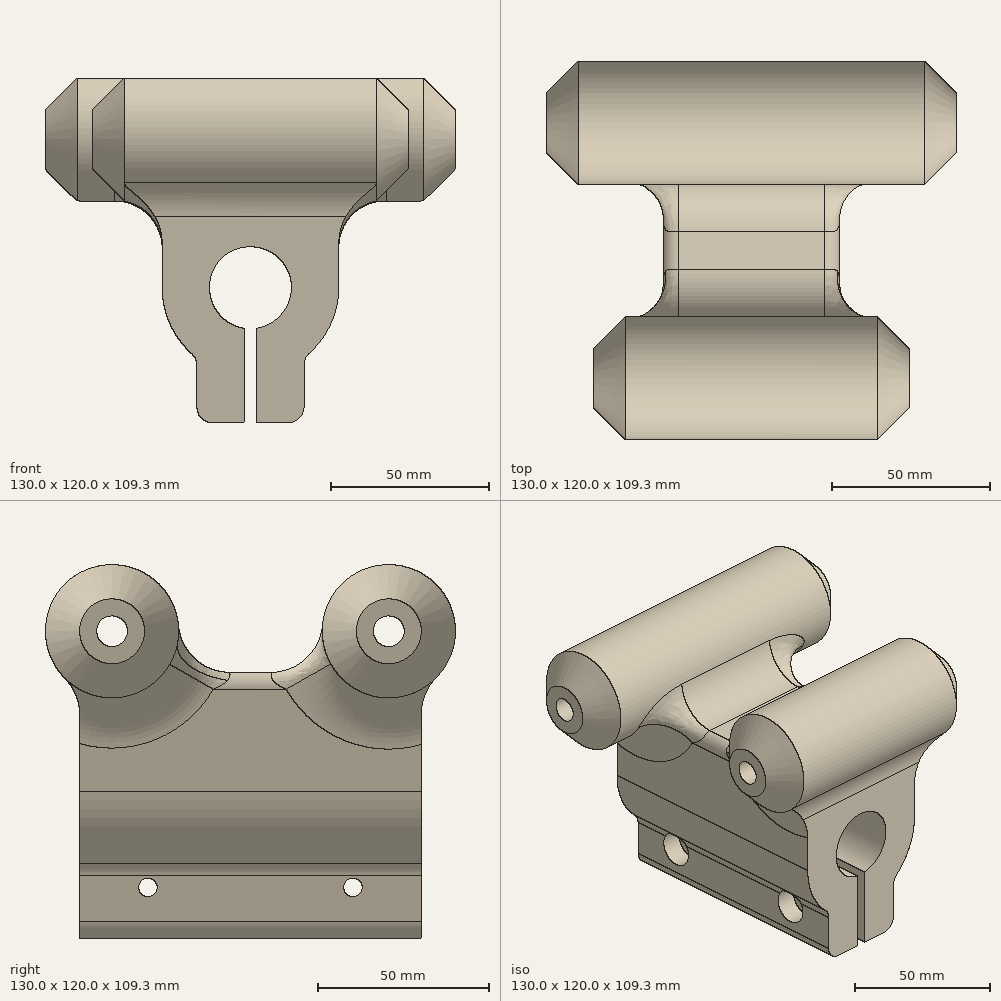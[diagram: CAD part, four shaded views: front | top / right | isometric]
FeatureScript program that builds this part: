
annotation { "Feature Type Name" : "Feature", "Feature Type Description" : "" }
export const myFeature = defineFeature(function(context is Context, id is Id, definition is map)
    precondition{}
    {
        {
            var Q0;
            Q0=qCreatedBy(makeId("Front.planeOp"),FACE);
            var sketch = newSketch(context, id + "F0", { "sketchPlane" : qUnion([Q0])});
            skCircle(sketch, "E0", {"center": v(0, 0) * mm, "radius": 12.5 * mm, "construction": true});
            skCircle(sketch, "E1", {"center": v(0, 0) * mm, "radius": 28 * mm, "construction": true});
            skCircle(sketch, "E2", {"center": v(0, 0) * mm, "radius": 13 * mm, "construction": true});
            skLineSegment(sketch, "E3", {"start": v(-28, 0) * mm, "end": v(-28, 30) * mm});
            skLineSegment(sketch, "E4", {"start": v(-23, 35) * mm, "end": v(23, 35) * mm});
            skLineSegment(sketch, "E5", {"start": v(28, 30) * mm, "end": v(28, 0) * mm});
            skPoint(sketch, "E6.visualSharp", {"position": v(-28, 35) * mm});
            skArc(sketch, "E6.filletArc", {"start": v(-23, 35) * mm, "mid": v(-26.54, 33.54) * mm, "end": v(-28, 30) * mm});
            skPoint(sketch, "E7.visualSharp", {"position": v(28, 35) * mm});
            skArc(sketch, "E7.filletArc", {"start": v(28, 30) * mm, "mid": v(26.54, 33.54) * mm, "end": v(23, 35) * mm});
            skLineSegment(sketch, "E8", {"start": v(-2, -12.85) * mm, "end": v(-2, -42.85) * mm});
            skLineSegment(sketch, "E9", {"start": v(-2, -42.85) * mm, "end": v(-12, -42.85) * mm});
            skLineSegment(sketch, "E10", {"start": v(-17, -37.85) * mm, "end": v(-17, -24.6) * mm});
            skLineSegment(sketch, "E11", {"start": v(0, 0) * mm, "end": v(0, -45.72) * mm, "construction": true});
            skLineSegment(sketch, "E12.MirrorCS", {"start": v(2, -12.85) * mm, "end": v(2, -42.85) * mm});
            skLineSegment(sketch, "E13.MirrorCS", {"start": v(2, -42.85) * mm, "end": v(12, -42.85) * mm});
            skLineSegment(sketch, "E14.MirrorCS", {"start": v(17, -37.85) * mm, "end": v(17, -24.6) * mm});
            skArc(sketch, "E15", {"start": v(-2, -12.85) * mm, "mid": v(0, 13) * mm, "end": v(2, -12.85) * mm});
            skArc(sketch, "E16", {"start": v(-28, 0) * mm, "mid": v(-25.56, -11.43) * mm, "end": v(-18.67, -20.87) * mm});
            skArc(sketch, "E17", {"start": v(28, 0) * mm, "mid": v(25.56, -11.43) * mm, "end": v(18.67, -20.87) * mm});
            skPoint(sketch, "E18.visualSharp", {"position": v(-17, -42.85) * mm});
            skArc(sketch, "E18.filletArc", {"start": v(-17, -37.85) * mm, "mid": v(-15.54, -41.38) * mm, "end": v(-12, -42.85) * mm});
            skPoint(sketch, "E19.visualSharp", {"position": v(17, -42.85) * mm});
            skArc(sketch, "E19.filletArc", {"start": v(12, -42.85) * mm, "mid": v(15.54, -41.38) * mm, "end": v(17, -37.85) * mm});
            skPoint(sketch, "E20.visualSharp", {"position": v(-17, -22.25) * mm});
            skArc(sketch, "E20.filletArc", {"start": v(-17, -24.6) * mm, "mid": v(-17.44, -22.56) * mm, "end": v(-18.67, -20.87) * mm});
            skPoint(sketch, "E21.visualSharp", {"position": v(17, -22.25) * mm});
            skArc(sketch, "E21.filletArc", {"start": v(18.67, -20.87) * mm, "mid": v(17.44, -22.56) * mm, "end": v(17, -24.6) * mm});
            skSolve(sketch);
        }
        {
            var Q0;
            Q0 = qSketchRegion(id + "F0", true);
            extrude(context, id + "F1", {"entities" : qUnion([Q0]), "depth" : 100 * mm, "offsetDistance" : 25 * mm});
        }
        {
            var Q0;
            Q0=makeQuery(id+"F1.opExtrude","SWEPT_FACE",FACE,{"disambiguationData":[OSD([sQuery(id+"F0.wireOp",EDGE,"E10")])]});
            var sketch = newSketch(context, id + "F2", { "sketchPlane" : qUnion([Q0])});
            skLineSegment(sketch, "E22", {"start": v(-8.1, -28) * mm, "end": v(126.77, -28) * mm, "construction": true});
            skCircle(sketch, "E23", {"center": v(20, -28) * mm, "radius": 6.5 * mm});
            skCircle(sketch, "E24", {"center": v(80, -28) * mm, "radius": 6.5 * mm});
            skSolve(sketch);
        }
        {
            var Q0;
            Q0 = qSketchRegion(id + "F2", true);
            extrude(context, id + "F3", {"entities" : qUnion([Q0]), "operationType" : NewBodyOperationType.REMOVE, "oppositeDirection" : true, "depth" : 8 * mm, "offsetDistance" : 25 * mm, "hasSecondDirection" : true, "secondDirectionOppositeDirection" : false, "secondDirectionDepth" : 25 * mm});
        }
        {
            var Q0;
            Q0=qCreatedBy(makeId("Right.planeOp"),FACE);
            var sketch = newSketch(context, id + "F4", { "sketchPlane" : qUnion([Q0])});
            skLineSegment(sketch, "E25", {"start": v(-110.2, -28) * mm, "end": v(24.67, -28) * mm, "construction": true});
            skCircle(sketch, "E26", {"center": v(-80, -28) * mm, "radius": 2.7 * mm});
            skCircle(sketch, "E27", {"center": v(-20, -28) * mm, "radius": 2.7 * mm});
            skSolve(sketch);
        }
        {
            var Q0;
            Q0 = qSketchRegion(id + "F4", true);
            extrude(context, id + "F5", {"entities" : qUnion([Q0]), "operationType" : NewBodyOperationType.REMOVE, "endBound" : BoundingType.THROUGH_ALL, "depth" : 25 * mm, "offsetDistance" : 25 * mm});
        }
        {
            var Q0;
            Q0=makeQuery(id+"F1.opExtrude","SWEPT_FACE",FACE,{"disambiguationData":[OSD([sQuery(id+"F0.wireOp",EDGE,"E10")])]});
            var sketch = newSketch(context, id + "F6", { "sketchPlane" : qUnion([Q0])});
            skCircle(sketch, "E28", {"center": v(20, -28) * mm, "radius": 3.5 * mm});
            skCircle(sketch, "E29", {"center": v(80, -28) * mm, "radius": 3.5 * mm});
            skSolve(sketch);
        }
        {
            var Q0;
            Q0 = qSketchRegion(id + "F6", true);
            var Q1;
            Q1=makeQuery(id+"F1.opExtrude","SWEPT_FACE",FACE,{"disambiguationData":[OSD([sQuery(id+"F0.wireOp",EDGE,"E8")])]});
            extrude(context, id + "F7", {"entities" : qUnion([Q0]), "operationType" : NewBodyOperationType.REMOVE, "endBound" : BoundingType.UP_TO_SURFACE, "oppositeDirection" : true, "depth" : 25 * mm, "endBoundEntityFace" : qUnion([Q1]), "offsetDistance" : 25 * mm});
        }
        {
            var Q0;
            Q0=makeQuery(id+"F1.opExtrude","SWEPT_FACE",FACE,{"disambiguationData":[OSD([sQuery(id+"F0.wireOp",EDGE,"E4")])]});
            cPlane(context, id + "F8", {"entities" : qUnion([Q0]), "cplaneType" : CPlaneType.OFFSET, "offset" : 12 * mm, "width" : 150 * mm, "height" : 150 * mm});
        }
        {
            var Q0;
            Q0=qCreatedBy(id+"F8.planeOp",FACE);
            var sketch = newSketch(context, id + "F9", { "sketchPlane" : qUnion([Q0])});
            skLineSegment(sketch, "E30.top", {"start": v(-50, -86) * mm, "end": v(50, -86) * mm});
            skLineSegment(sketch, "E30.left", {"start": v(-50, -81) * mm, "end": v(-50, -86) * mm});
            skLineSegment(sketch, "E30.right", {"start": v(50, -81) * mm, "end": v(50, -86) * mm});
            skLineSegment(sketch, "E31", {"start": v(-55.3, -90.5) * mm, "end": v(55.16, -90.5) * mm, "construction": true});
            skLineSegment(sketch, "E32", {"start": v(-50, -81) * mm, "end": v(-40, -71) * mm});
            skLineSegment(sketch, "E33", {"start": v(-40, -71) * mm, "end": v(40, -71) * mm});
            skLineSegment(sketch, "E34", {"start": v(40, -71) * mm, "end": v(50, -81) * mm});
            skSolve(sketch);
        }
        {
            var Q0;
            Q0 = qSketchRegion(id + "F9", true);
            var Q1;
            Q1=sQuery(id+"F9.wireOp",EDGE,"E31");
            revolve(context, id + "F10", {"operationType" : NewBodyOperationType.ADD, "surfaceOperationType" : NewSurfaceOperationType.NEW, "entities" : qUnion([Q0]), "axis" : qUnion([Q1]), "revolveType" : RevolveType.FULL});
        }
        {
            var Q0;
            Q0=qCreatedBy(id+"F8.planeOp",FACE);
            var sketch = newSketch(context, id + "F11", { "sketchPlane" : qUnion([Q0])});
            skLineSegment(sketch, "E35", {"start": v(-53.78, -9.5) * mm, "end": v(60.6, -9.5) * mm, "construction": true});
            skLineSegment(sketch, "E36", {"start": v(-65, -14) * mm, "end": v(65, -14) * mm});
            skLineSegment(sketch, "E37", {"start": v(65, -14) * mm, "end": v(65, -19) * mm});
            skLineSegment(sketch, "E38", {"start": v(65, -19) * mm, "end": v(55, -29) * mm});
            skLineSegment(sketch, "E39", {"start": v(55, -29) * mm, "end": v(-55, -29) * mm});
            skLineSegment(sketch, "E40", {"start": v(-55, -29) * mm, "end": v(-65, -19) * mm});
            skLineSegment(sketch, "E41", {"start": v(-65, -19) * mm, "end": v(-65, -14) * mm});
            skSolve(sketch);
        }
        {
            var Q0;
            Q0 = qSketchRegion(id + "F11", true);
            var Q1;
            Q1=sQuery(id+"F11.wireOp",EDGE,"E35");
            revolve(context, id + "F12", {"operationType" : NewBodyOperationType.ADD, "surfaceOperationType" : NewSurfaceOperationType.NEW, "entities" : qUnion([Q0]), "axis" : qUnion([Q1]), "revolveType" : RevolveType.FULL});
        }
        {
            var Q0;
            Q0=makeQuery(id+"F12.boolean.opBoolean","INTERSECT",EDGE,{"derivedFrom":[makeQuery(id+"F1.opExtrude","SWEPT_FACE",FACE,{"disambiguationData":[OSD([sQuery(id+"F0.wireOp",EDGE,"E4")])]}),makeQuery(id+"F12.opRevolve","SWEPT_FACE",FACE,{"disambiguationData":[OSD([sQuery(id+"F11.wireOp",EDGE,"E39")])]})]});
            var Q1;
            Q1=makeQuery(id+"F12.boolean.opBoolean","INTERSECT",EDGE,{"derivedFrom":[makeQuery(id+"F1.opExtrude","CAP_FACE",FACE,{"disambiguationData":[OSD([sQuery(id+"F0.wireOp",EDGE,"E3"),sQuery(id+"F0.wireOp",EDGE,"E4"),sQuery(id+"F0.wireOp",EDGE,"E5"),sQuery(id+"F0.wireOp",EDGE,"E6.filletArc"),sQuery(id+"F0.wireOp",EDGE,"E7.filletArc"),sQuery(id+"F0.wireOp",EDGE,"E8"),sQuery(id+"F0.wireOp",EDGE,"E9"),sQuery(id+"F0.wireOp",EDGE,"E10"),sQuery(id+"F0.wireOp",EDGE,"E12.MirrorCS"),sQuery(id+"F0.wireOp",EDGE,"E13.MirrorCS"),sQuery(id+"F0.wireOp",EDGE,"E14.MirrorCS"),sQuery(id+"F0.wireOp",EDGE,"E15"),sQuery(id+"F0.wireOp",EDGE,"E16"),sQuery(id+"F0.wireOp",EDGE,"E17"),sQuery(id+"F0.wireOp",EDGE,"E18.filletArc"),sQuery(id+"F0.wireOp",EDGE,"E19.filletArc"),sQuery(id+"F0.wireOp",EDGE,"E20.filletArc"),sQuery(id+"F0.wireOp",EDGE,"E21.filletArc")])],"isStart":true}),makeQuery(id+"F12.opRevolve","SWEPT_FACE",FACE,{"disambiguationData":[OSD([sQuery(id+"F11.wireOp",EDGE,"E39")])]})]});
            var Q2;
            Q2=makeQuery(id+"F10.boolean.opBoolean","INTERSECT",EDGE,{"derivedFrom":[makeQuery(id+"F1.opExtrude","SWEPT_FACE",FACE,{"disambiguationData":[OSD([sQuery(id+"F0.wireOp",EDGE,"E4")])]}),makeQuery(id+"F10.opRevolve","SWEPT_FACE",FACE,{"disambiguationData":[OSD([sQuery(id+"F9.wireOp",EDGE,"E33")])]})]});
            var Q3;
            Q3=makeQuery(id+"F10.boolean.opBoolean","INTERSECT",EDGE,{"derivedFrom":[makeQuery(id+"F1.opExtrude","CAP_FACE",FACE,{"disambiguationData":[OSD([sQuery(id+"F0.wireOp",EDGE,"E3"),sQuery(id+"F0.wireOp",EDGE,"E4"),sQuery(id+"F0.wireOp",EDGE,"E5"),sQuery(id+"F0.wireOp",EDGE,"E6.filletArc"),sQuery(id+"F0.wireOp",EDGE,"E7.filletArc"),sQuery(id+"F0.wireOp",EDGE,"E8"),sQuery(id+"F0.wireOp",EDGE,"E9"),sQuery(id+"F0.wireOp",EDGE,"E10"),sQuery(id+"F0.wireOp",EDGE,"E12.MirrorCS"),sQuery(id+"F0.wireOp",EDGE,"E13.MirrorCS"),sQuery(id+"F0.wireOp",EDGE,"E14.MirrorCS"),sQuery(id+"F0.wireOp",EDGE,"E15"),sQuery(id+"F0.wireOp",EDGE,"E16"),sQuery(id+"F0.wireOp",EDGE,"E17"),sQuery(id+"F0.wireOp",EDGE,"E18.filletArc"),sQuery(id+"F0.wireOp",EDGE,"E19.filletArc"),sQuery(id+"F0.wireOp",EDGE,"E20.filletArc"),sQuery(id+"F0.wireOp",EDGE,"E21.filletArc")])],"isStart":false}),makeQuery(id+"F10.opRevolve","SWEPT_FACE",FACE,{"disambiguationData":[OSD([sQuery(id+"F9.wireOp",EDGE,"E33")])]})]});
            fillet(context, id + "F13", {"entities" : qUnion([Q0, Q1, Q2, Q3]), "radius" : 15 * mm, "tangentPropagation" : true, "allowEdgeOverflow" : false});
        }
    });
